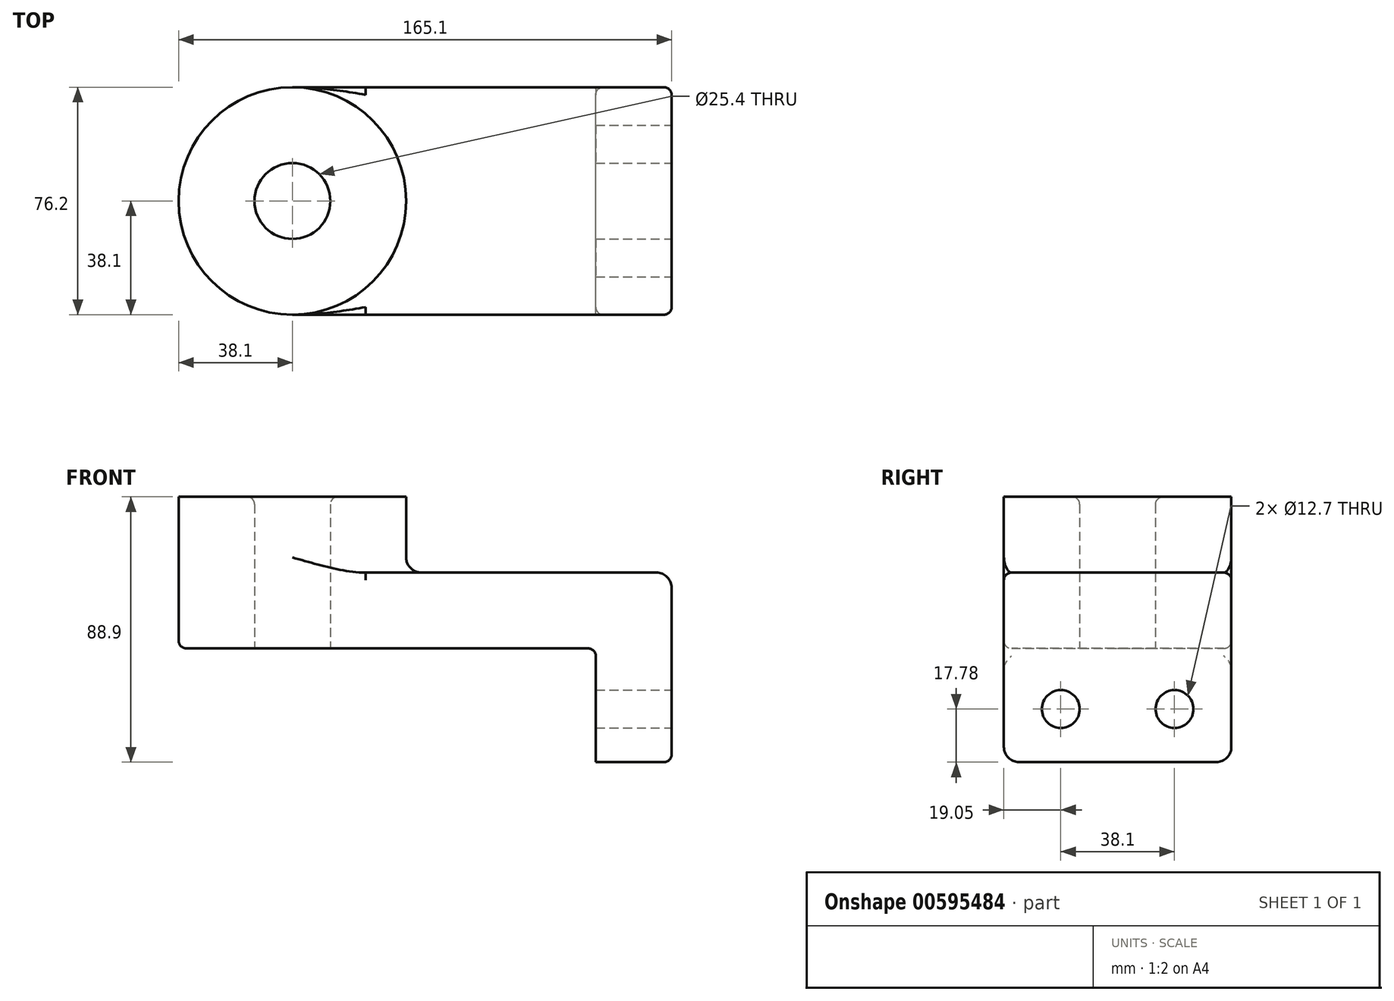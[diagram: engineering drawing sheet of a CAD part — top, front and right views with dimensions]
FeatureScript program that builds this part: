
annotation { "Feature Type Name" : "Feature", "Feature Type Description" : "" }
export const myFeature = defineFeature(function(context is Context, id is Id, definition is map)
    precondition{}
    {
        {
            var Q0;
            Q0=qCreatedBy(makeId("Top.planeOp"),FACE);
            var sketch = newSketch(context, id + "F0", { "sketchPlane" : qUnion([Q0])});
            skLineSegment(sketch, "E0.bottom", {"start": v(-63.5, -38.1) * mm, "end": v(63.5, -38.1) * mm});
            skLineSegment(sketch, "E0.top", {"start": v(-63.5, 38.1) * mm, "end": v(63.5, 38.1) * mm});
            skLineSegment(sketch, "E0.left", {"start": v(-63.5, -38.1) * mm, "end": v(-63.5, 38.1) * mm});
            skLineSegment(sketch, "E0.right", {"start": v(63.5, -38.1) * mm, "end": v(63.5, 38.1) * mm});
            skPoint(sketch, "E0.middle", {"position": v(0, 0) * mm});
            skCircle(sketch, "E1", {"center": v(-63.5, 0) * mm, "radius": 38.1 * mm});
            skCircle(sketch, "E2", {"center": v(-63.5, 0) * mm, "radius": 12.7 * mm});
            skSolve(sketch);
        }
        {
            var Q0;
            Q0 = qSketchRegion(id + "F0", true);
            extrude(context, id + "F1", {"entities" : qUnion([Q0]), "depth" : 25.4 * mm, "offsetDistance" : 25.4 * mm});
        }
        {
            var Q0;
            {var subQ1=sQuery(id+"F0.wireOp",EDGE,"E0.left");var subQ3=sQuery(id+"F0.wireOp",EDGE,"E2");var subQ4=makeQuery(id+"F0.imprint","INTERSECT",VERTEX,{"disambiguationData":[OD(0.0)],"derivedFrom":[subQ1,subQ3]});Q0=makeQuery(id+"F0.imprint","IMPRINT",FACE,{"disambiguationData":[TD([[makeQuery(id+"F0.imprint","IMPRINT",EDGE,{"disambiguationData":[TD([[subQ4,1.0]])],"derivedFrom":subQ3}),-1.0]])]});}
            var Q1;
            {var subQ1=sQuery(id+"F0.wireOp",EDGE,"E0.left");var subQ3=sQuery(id+"F0.wireOp",EDGE,"E2");var subQ4=makeQuery(id+"F0.imprint","INTERSECT",VERTEX,{"disambiguationData":[OD(0.0)],"derivedFrom":[subQ1,subQ3]});Q1=makeQuery(id+"F0.imprint","IMPRINT",FACE,{"disambiguationData":[TD([[makeQuery(id+"F0.imprint","IMPRINT",EDGE,{"disambiguationData":[TD([[subQ4,-1.0]])],"derivedFrom":subQ3}),-1.0]])]});}
            extrude(context, id + "F2", {"entities" : qUnion([Q0, Q1]), "operationType" : NewBodyOperationType.ADD, "depth" : 50.8 * mm, "offsetDistance" : 25.4 * mm});
        }
        {
            var Q0;
            Q0=makeQuery(id+"F1.opExtrude","SWEPT_FACE",FACE,{"disambiguationData":[OSD([sQuery(id+"F0.wireOp",EDGE,"E0.right")])]});
            var sketch = newSketch(context, id + "F3", { "sketchPlane" : qUnion([Q0])});
            skLineSegment(sketch, "E3.bottom", {"start": v(-38.1, 25.4) * mm, "end": v(38.1, 25.4) * mm});
            skLineSegment(sketch, "E3.top", {"start": v(-38.1, -38.1) * mm, "end": v(38.1, -38.1) * mm});
            skLineSegment(sketch, "E3.left", {"start": v(-38.1, 25.4) * mm, "end": v(-38.1, -38.1) * mm});
            skLineSegment(sketch, "E3.right", {"start": v(38.1, 25.4) * mm, "end": v(38.1, -38.1) * mm});
            skCircle(sketch, "E4", {"center": v(-19.05, -20.32) * mm, "radius": 6.35 * mm});
            skLineSegment(sketch, "E5", {"start": v(0, 0) * mm, "end": v(0, -38.1) * mm, "construction": true});
            skCircle(sketch, "E6.MirrorC", {"center": v(19.05, -20.32) * mm, "radius": 6.35 * mm});
            skSolve(sketch);
        }
        {
            var Q0;
            Q0 = qSketchRegion(id + "F3", true);
            extrude(context, id + "F4", {"entities" : qUnion([Q0]), "operationType" : NewBodyOperationType.ADD, "oppositeDirection" : true, "depth" : 25.4 * mm, "offsetDistance" : 25.4 * mm});
        }
        {
            var Q0;
            {var subQ0=sQuery(id+"F0.wireOp",EDGE,"E1");Q0=makeQuery(id+"F2.boolean.opBoolean","INTERSECT",EDGE,{"derivedFrom":[makeQuery(id+"F1.opExtrude","CAP_FACE",FACE,{"disambiguationData":[OSD([sQuery(id+"F0.wireOp",EDGE,"E0.bottom"),sQuery(id+"F0.wireOp",EDGE,"E0.top"),sQuery(id+"F0.wireOp",EDGE,"E0.right"),subQ0,sQuery(id+"F0.wireOp",EDGE,"E2")])],"isStart":false}),makeQuery(id+"F2.opExtrude","SWEPT_FACE",FACE,{"disambiguationData":[OSD([subQ0])]})]});}
            var Q1;
            Q1=makeQuery(id+"F1.opExtrude","CAP_EDGE",EDGE,{"disambiguationData":[OSD([sQuery(id+"F0.wireOp",EDGE,"E0.right")])],"isStart":false});
            var Q2;
            Q2=makeQuery(id+"F4.opExtrude","SWEPT_EDGE",EDGE,{"disambiguationData":[OSD([sQuery(id+"F3.wireOp",EDGE,"E3.top"),sQuery(id+"F3.wireOp",EDGE,"E3.left")])]});
            var Q3;
            Q3=makeQuery(id+"F4.opExtrude","SWEPT_EDGE",EDGE,{"disambiguationData":[OSD([sQuery(id+"F3.wireOp",EDGE,"E3.top"),sQuery(id+"F3.wireOp",EDGE,"E3.right")])]});
            fillet(context, id + "F5", {"entities" : qUnion([Q0, Q1, Q2, Q3]), "radius" : 5.08 * mm, "tangentPropagation" : true, "allowEdgeOverflow" : false});
        }
        {
            var Q0;
            Q0=makeQuery(id+"F1.opExtrude","CAP_EDGE",EDGE,{"disambiguationData":[OSD([sQuery(id+"F0.wireOp",EDGE,"E0.bottom")])],"isStart":false});
            var Q1;
            Q1=makeQuery(id+"F4.boolean.opBoolean","INTERSECT",EDGE,{"derivedFrom":[makeQuery(id+"F1.opExtrude","CAP_FACE",FACE,{"disambiguationData":[OSD([sQuery(id+"F0.wireOp",EDGE,"E0.bottom"),sQuery(id+"F0.wireOp",EDGE,"E0.top"),sQuery(id+"F0.wireOp",EDGE,"E0.right"),sQuery(id+"F0.wireOp",EDGE,"E1"),sQuery(id+"F0.wireOp",EDGE,"E2")])],"isStart":true}),makeQuery(id+"F4.opExtrude","CAP_FACE",FACE,{"disambiguationData":[OSD([sQuery(id+"F3.wireOp",EDGE,"E3.bottom"),sQuery(id+"F3.wireOp",EDGE,"E3.top"),sQuery(id+"F3.wireOp",EDGE,"E3.left"),sQuery(id+"F3.wireOp",EDGE,"E3.right"),sQuery(id+"F3.wireOp",EDGE,"E6.MirrorC"),sQuery(id+"F3.wireOp",EDGE,"E4")])],"isStart":false})]});
            var Q2;
            Q2=makeQuery(id+"F1.opExtrude","CAP_EDGE",EDGE,{"disambiguationData":[OSD([sQuery(id+"F0.wireOp",EDGE,"E0.bottom")])],"isStart":true});
            var Q3;
            Q3=makeQuery(id+"F2.opExtrude","CAP_EDGE",EDGE,{"disambiguationData":[OSD([sQuery(id+"F0.wireOp",EDGE,"E2")])],"isStart":false});
            fillet(context, id + "F6", {"entities" : qUnion([Q0, Q1, Q2, Q3]), "radius" : 2.54 * mm, "tangentPropagation" : true, "allowEdgeOverflow" : false});
        }
    });
